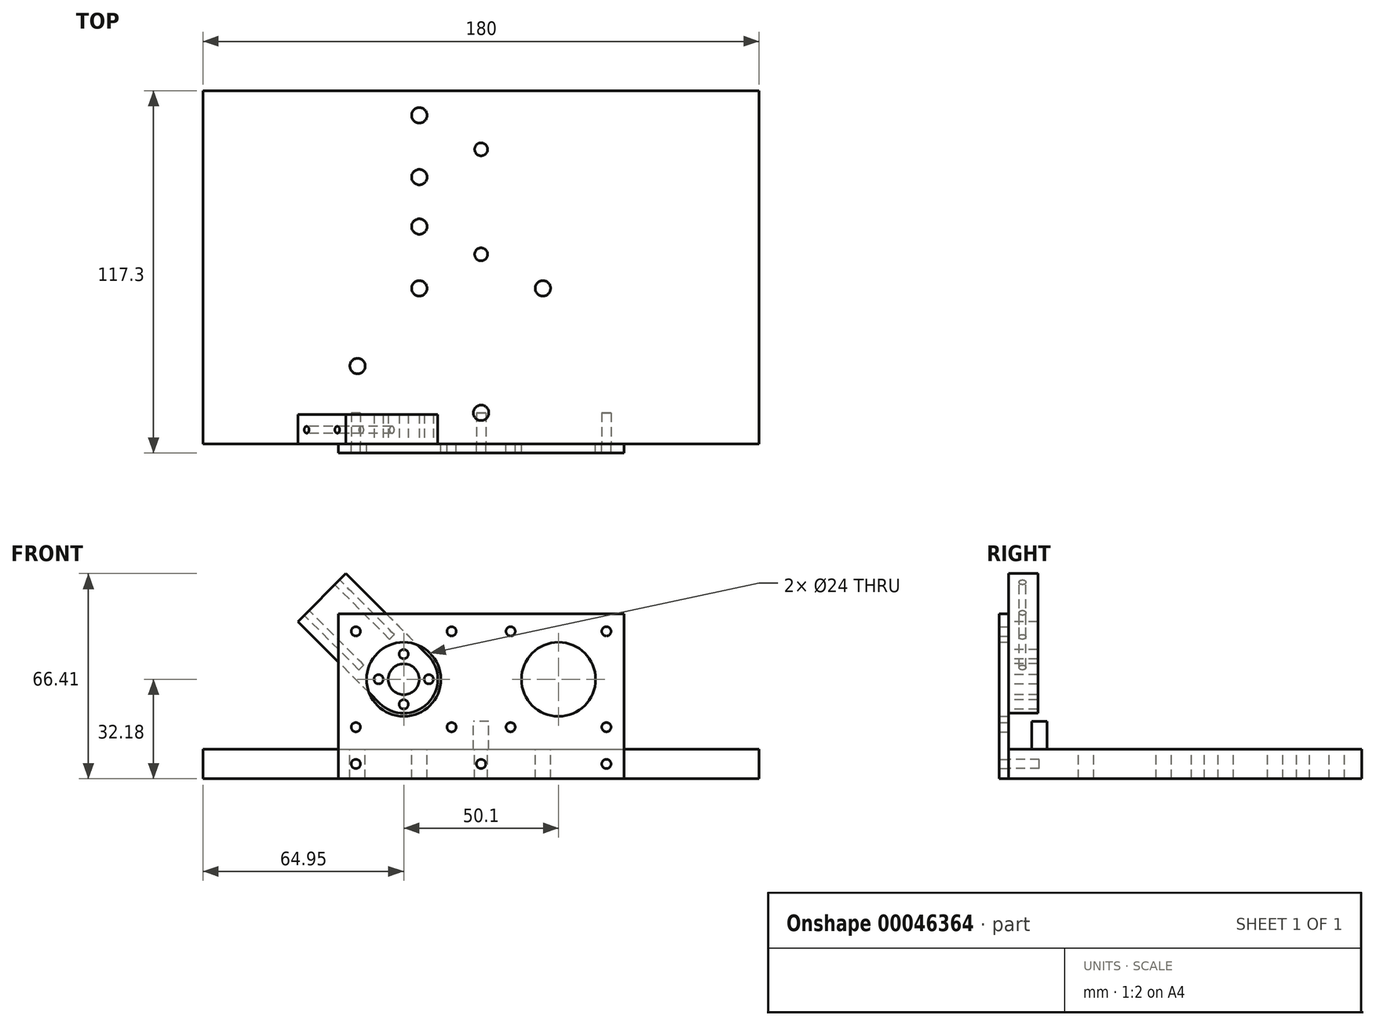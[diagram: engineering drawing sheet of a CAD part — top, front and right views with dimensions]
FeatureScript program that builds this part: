
annotation { "Feature Type Name" : "Feature", "Feature Type Description" : "" }
export const myFeature = defineFeature(function(context is Context, id is Id, definition is map)
    precondition{}
    {
        {
            var Q0;
            Q0=qCreatedBy(makeId("Front.planeOp"),FACE);
            var sketch = newSketch(context, id + "F0", { "sketchPlane" : qUnion([Q0])});
            skLineSegment(sketch, "E0", {"start": v(-110.98, 0) * mm, "end": v(110.98, 0) * mm});
            skLineSegment(sketch, "E1", {"start": v(110.98, 0) * mm, "end": v(3.5, 107.48) * mm});
            skLineSegment(sketch, "E2", {"start": v(3.5, 107.48) * mm, "end": v(-3.5, 107.48) * mm, "construction": true});
            skLineSegment(sketch, "E3", {"start": v(-3.5, 107.48) * mm, "end": v(-110.98, 0) * mm});
            skLineSegment(sketch, "E4", {"start": v(0, 0) * mm, "end": v(0, 107.48) * mm, "construction": true});
            skLineSegment(sketch, "E5", {"start": v(3.5, 107.48) * mm, "end": v(5.62, 109.6) * mm});
            skLineSegment(sketch, "E6", {"start": v(5.62, 109.6) * mm, "end": v(113.1, 2.12) * mm});
            skLineSegment(sketch, "E7", {"start": v(113.1, 2.12) * mm, "end": v(110.98, 0) * mm});
            skLineSegment(sketch, "E8", {"start": v(5.62, 109.6) * mm, "end": v(9.86, 113.84) * mm, "construction": true});
            skLineSegment(sketch, "E9", {"start": v(9.86, 113.84) * mm, "end": v(117.34, 6.36) * mm, "construction": true});
            skLineSegment(sketch, "E10", {"start": v(117.34, 6.36) * mm, "end": v(113.1, 2.12) * mm, "construction": true});
            skLineSegment(sketch, "E11.0.MirrorCS", {"start": v(-113.1, 2.12) * mm, "end": v(-110.98, 0) * mm});
            skLineSegment(sketch, "E11.1.MirrorCS", {"start": v(-117.34, 6.36) * mm, "end": v(-113.1, 2.12) * mm, "construction": true});
            skLineSegment(sketch, "E11.2.MirrorCS", {"start": v(-5.62, 109.6) * mm, "end": v(-9.86, 113.84) * mm, "construction": true});
            skLineSegment(sketch, "E11.3.MirrorCS", {"start": v(-9.86, 113.84) * mm, "end": v(-117.34, 6.36) * mm, "construction": true});
            skLineSegment(sketch, "E11.4.MirrorCS", {"start": v(-5.62, 109.6) * mm, "end": v(-113.1, 2.12) * mm});
            skLineSegment(sketch, "E11.5.MirrorCS", {"start": v(-3.5, 107.48) * mm, "end": v(-5.62, 109.6) * mm});
            skLineSegment(sketch, "E12", {"start": v(48.75, 66.47) * mm, "end": v(53, 70.71) * mm, "construction": true});
            skLineSegment(sketch, "E13.0.MirrorCS", {"start": v(-48.75, 66.47) * mm, "end": v(-53, 70.71) * mm, "construction": true});
            skLineSegment(sketch, "E14", {"start": v(97.55, 17.68) * mm, "end": v(101.79, 21.92) * mm, "construction": true});
            skLineSegment(sketch, "E15.0.MirrorCS", {"start": v(-97.55, 17.68) * mm, "end": v(-101.79, 21.92) * mm, "construction": true});
            skLineSegment(sketch, "E16", {"start": v(5.62, 109.6) * mm, "end": v(-9.86, 125.09) * mm, "construction": true});
            skLineSegment(sketch, "E17", {"start": v(-5.62, 109.6) * mm, "end": v(9.86, 125.09) * mm, "construction": true});
            skLineSegment(sketch, "E18", {"start": v(-3.5, 107.48) * mm, "end": v(-3.5, 118.8) * mm, "construction": true});
            skLineSegment(sketch, "E19", {"start": v(-9.86, 113.84) * mm, "end": v(-4.2, 119.5) * mm, "construction": true});
            skLineSegment(sketch, "E20", {"start": v(-4.2, 119.5) * mm, "end": v(-3.5, 118.8) * mm, "construction": true});
            skLineSegment(sketch, "E21.0.MirrorCS", {"start": v(3.5, 107.48) * mm, "end": v(3.5, 118.8) * mm, "construction": true});
            skLineSegment(sketch, "E21.1.MirrorCS", {"start": v(4.2, 119.5) * mm, "end": v(3.5, 118.8) * mm, "construction": true});
            skLineSegment(sketch, "E21.2.MirrorCS", {"start": v(9.86, 113.84) * mm, "end": v(4.2, 119.5) * mm, "construction": true});
            skLineSegment(sketch, "E22", {"start": v(-84.7, 9.31) * mm, "end": v(-28.13, 65.88) * mm, "construction": true});
            skPoint(sketch, "E23", {"position": v(-56.41, 37.6) * mm});
            skPoint(sketch, "E24", {"position": v(-57.24, 53.74) * mm});
            skLineSegment(sketch, "E25", {"start": v(-33.43, 60.58) * mm, "end": v(-90, 4) * mm, "construction": true});
            skLineSegment(sketch, "E26", {"start": v(-90, 4) * mm, "end": v(-10, 4) * mm, "construction": true});
            skLineSegment(sketch, "E27", {"start": v(-10, 4) * mm, "end": v(-10, 13) * mm});
            skLineSegment(sketch, "E28", {"start": v(-10, 13) * mm, "end": v(-68.27, 13) * mm, "construction": true});
            skLineSegment(sketch, "E29", {"start": v(-68.27, 13) * mm, "end": v(-27.07, 54.21) * mm, "construction": true});
            skLineSegment(sketch, "E30", {"start": v(-27.07, 54.21) * mm, "end": v(-33.43, 60.58) * mm, "construction": true});
            skLineSegment(sketch, "E31", {"start": v(-28.13, 65.88) * mm, "end": v(-36.61, 74.37) * mm, "construction": true});
            skLineSegment(sketch, "E32", {"start": v(-84.7, 9.31) * mm, "end": v(-93.18, 17.8) * mm, "construction": true});
            skLineSegment(sketch, "E33", {"start": v(-93.18, 17.8) * mm, "end": v(-36.61, 74.37) * mm, "construction": true});
            skLineSegment(sketch, "E34.0.MirrorCS", {"start": v(10, 4) * mm, "end": v(10, 13) * mm});
            skLineSegment(sketch, "E35", {"start": v(-10, 13) * mm, "end": v(10, 13) * mm});
            skLineSegment(sketch, "E36", {"start": v(-10, 4) * mm, "end": v(10, 4) * mm});
            skLineSegment(sketch, "E37.0.MirrorCS", {"start": v(68.27, 13) * mm, "end": v(27.07, 54.21) * mm, "construction": true});
            skLineSegment(sketch, "E37.1.MirrorCS", {"start": v(27.07, 54.21) * mm, "end": v(33.43, 60.58) * mm, "construction": true});
            skLineSegment(sketch, "E37.2.MirrorCS", {"start": v(33.43, 60.58) * mm, "end": v(90, 4) * mm, "construction": true});
            skLineSegment(sketch, "E37.3.MirrorCS", {"start": v(90, 4) * mm, "end": v(10, 4) * mm, "construction": true});
            skLineSegment(sketch, "E37.4.MirrorCS", {"start": v(10, 13) * mm, "end": v(68.27, 13) * mm, "construction": true});
            skPoint(sketch, "E38", {"position": v(-20, 13) * mm});
            skPoint(sketch, "E39.0.MirrorP", {"position": v(20, 13) * mm});
            skLineSegment(sketch, "E40.bottom", {"start": v(-90, 4) * mm, "end": v(90, 4) * mm});
            skLineSegment(sketch, "E40.top", {"start": v(-90, -5.52) * mm, "end": v(90, -5.52) * mm});
            skLineSegment(sketch, "E40.left", {"start": v(-90, 4) * mm, "end": v(-90, -5.52) * mm});
            skLineSegment(sketch, "E40.right", {"start": v(90, 4) * mm, "end": v(90, -5.52) * mm});
            skLineSegment(sketch, "E41", {"start": v(-50.76, 60.22) * mm, "end": v(-42.27, 51.74) * mm, "construction": true});
            skSolve(sketch);
        }
        {
            var Q0;
            {var subQ2=sQuery(id+"F0.wireOp",EDGE,"E27");Q0=makeQuery(id+"F0.imprint","IMPRINT",FACE,{"disambiguationData":[TD([[makeQuery(id+"F0.imprint","IMPRINT",EDGE,{"derivedFrom":subQ2}),-1.0]])]});}
            var Q1;
            {var subQ8=sQuery(id+"F0.wireOp",EDGE,"E34.0.MirrorCS");Q1=makeQuery(id+"F0.imprint","IMPRINT",FACE,{"disambiguationData":[TD([[makeQuery(id+"F0.imprint","IMPRINT",EDGE,{"derivedFrom":subQ8}),1.0]])]});}
            extrude(context, id + "F1", {"entities" : qUnion([Q0, Q1]), "oppositeDirection" : true, "depth" : 54 * mm});
        }
        {
            var Q0;
            {var subQ3=sQuery(id+"F0.wireOp",EDGE,"E40.top");Q0=makeQuery(id+"F0.imprint","IMPRINT",FACE,{"disambiguationData":[TD([[makeQuery(id+"F0.imprint","IMPRINT",EDGE,{"derivedFrom":subQ3}),1.0]])]});}
            var Q1;
            {var subQ1=sQuery(id+"F0.wireOp",EDGE,"E0");var subQ5=sQuery(id+"F0.wireOp",EDGE,"E40.left");var subQ6=makeQuery(id+"F0.imprint","INTERSECT",VERTEX,{"derivedFrom":[subQ1,subQ5]});Q1=makeQuery(id+"F0.imprint","IMPRINT",FACE,{"disambiguationData":[TD([[makeQuery(id+"F0.imprint","IMPRINT",EDGE,{"disambiguationData":[TD([[subQ6,-1.0]])],"derivedFrom":subQ1}),1.0]])]});}
            extrude(context, id + "F2", {"entities" : qUnion([Q0, Q1]), "oppositeDirection" : true, "depth" : 114.3 * mm});
        }
        {
            var Q0;
            Q0=makeQuery(id+"F1.opExtrude","SWEPT_FACE",FACE,{"disambiguationData":[OSD([sQuery(id+"F0.wireOp",EDGE,"E35")])]});
            var sketch = newSketch(context, id + "F3", { "sketchPlane" : qUnion([Q0])});
            skCircle(sketch, "E42", {"center": v(20, 50.3) * mm, "radius": 2.5 * mm});
            skCircle(sketch, "E43", {"center": v(-20, 50.3) * mm, "radius": 2.5 * mm});
            skLineSegment(sketch, "E44", {"start": v(0, 0) * mm, "end": v(0, 54) * mm, "construction": true});
            skLineSegment(sketch, "E45", {"start": v(-10, 27) * mm, "end": v(10, 27) * mm, "construction": true});
            skCircle(sketch, "E46", {"center": v(-20, 70.3) * mm, "radius": 2.5 * mm});
            skCircle(sketch, "E47", {"center": v(-20, 86.3) * mm, "radius": 2.5 * mm});
            skCircle(sketch, "E48", {"center": v(-20, 106.3) * mm, "radius": 2.5 * mm});
            skCircle(sketch, "E49.0.MirrorC", {"center": v(20, 70.3) * mm, "radius": 2.5 * mm});
            skCircle(sketch, "E49.1.MirrorC", {"center": v(20, 86.3) * mm, "radius": 2.5 * mm});
            skCircle(sketch, "E49.2.MirrorC", {"center": v(20, 106.3) * mm, "radius": 2.5 * mm});
            skCircle(sketch, "E50", {"center": v(-40, 25.15) * mm, "radius": 2.5 * mm});
            skLineSegment(sketch, "E51", {"start": v(-20, 50.3) * mm, "end": v(-20, 0) * mm, "construction": true});
            skPoint(sketch, "E52", {"position": v(-20, 25.15) * mm});
            skLineSegment(sketch, "E53", {"start": v(20, 86.3) * mm, "end": v(20, 70.3) * mm, "construction": true});
            skLineSegment(sketch, "E54", {"start": v(-20, 86.3) * mm, "end": v(-20, 70.3) * mm, "construction": true});
            skLineSegment(sketch, "E55", {"start": v(-20, 78.3) * mm, "end": v(20, 78.3) * mm, "construction": true});
            skCircle(sketch, "E56", {"center": v(0, 95.3) * mm, "radius": 2.1 * mm});
            skCircle(sketch, "E57", {"center": v(0, 61.3) * mm, "radius": 2.1 * mm});
            skSolve(sketch);
        }
        {
            var Q0;
            Q0=makeQuery(id+"F3.imprint","IMPRINT",FACE,{"disambiguationData":[TD([[makeQuery(id+"F3.imprint","IMPRINT",EDGE,{"derivedFrom":sQuery(id+"F3.wireOp",EDGE,"E43")}),1.0]])]});
            var Q1;
            Q1=makeQuery(id+"F3.imprint","IMPRINT",FACE,{"disambiguationData":[TD([[makeQuery(id+"F3.imprint","IMPRINT",EDGE,{"derivedFrom":sQuery(id+"F3.wireOp",EDGE,"c1587aed-859c-4511-8a7d-6d54e1cc8fba")}),1.0]])]});
            var Q2;
            Q2=makeQuery(id+"F3.imprint","IMPRINT",FACE,{"disambiguationData":[TD([[makeQuery(id+"F3.imprint","IMPRINT",EDGE,{"derivedFrom":sQuery(id+"F3.wireOp",EDGE,"E42")}),1.0]])]});
            var Q3;
            Q3=makeQuery(id+"F3.imprint","IMPRINT",FACE,{"disambiguationData":[TD([[makeQuery(id+"F3.imprint","IMPRINT",EDGE,{"derivedFrom":sQuery(id+"F3.wireOp",EDGE,"E46")}),1.0]])]});
            var Q4;
            Q4=makeQuery(id+"F3.imprint","IMPRINT",FACE,{"disambiguationData":[TD([[makeQuery(id+"F3.imprint","IMPRINT",EDGE,{"derivedFrom":sQuery(id+"F3.wireOp",EDGE,"E47")}),1.0]])]});
            var Q5;
            Q5=makeQuery(id+"F3.imprint","IMPRINT",FACE,{"disambiguationData":[TD([[makeQuery(id+"F3.imprint","IMPRINT",EDGE,{"derivedFrom":sQuery(id+"F3.wireOp",EDGE,"E48")}),1.0]])]});
            var Q6;
            Q6=makeQuery(id+"F3.imprint","IMPRINT",FACE,{"disambiguationData":[TD([[makeQuery(id+"F3.imprint","IMPRINT",EDGE,{"derivedFrom":sQuery(id+"F3.wireOp",EDGE,"E49.2.MirrorC")}),-1.0]])]});
            var Q7;
            Q7=makeQuery(id+"F3.imprint","IMPRINT",FACE,{"disambiguationData":[TD([[makeQuery(id+"F3.imprint","IMPRINT",EDGE,{"derivedFrom":sQuery(id+"F3.wireOp",EDGE,"E49.1.MirrorC")}),-1.0]])]});
            var Q8;
            Q8=makeQuery(id+"F3.imprint","IMPRINT",FACE,{"disambiguationData":[TD([[makeQuery(id+"F3.imprint","IMPRINT",EDGE,{"derivedFrom":sQuery(id+"F3.wireOp",EDGE,"E49.0.MirrorC")}),-1.0]])]});
            var Q9;
            Q9=makeQuery(id+"F3.imprint","IMPRINT",FACE,{"disambiguationData":[TD([[makeQuery(id+"F3.imprint","IMPRINT",EDGE,{"derivedFrom":sQuery(id+"F3.wireOp",EDGE,"E50")}),1.0]])]});
            var Q10;
            Q10=makeQuery(id+"F3.imprint","IMPRINT",FACE,{"disambiguationData":[TD([[makeQuery(id+"F3.imprint","IMPRINT",EDGE,{"derivedFrom":sQuery(id+"F3.wireOp",EDGE,"4af6d40a-a213-410c-9ecb-ddd685a41705.0.MirrorC")}),-1.0]])]});
            var Q11;
            Q11=makeQuery(id+"F3.imprint","IMPRINT",FACE,{"disambiguationData":[TD([[makeQuery(id+"F3.imprint","IMPRINT",EDGE,{"derivedFrom":sQuery(id+"F3.wireOp",EDGE,"E56")}),1.0]])]});
            var Q12;
            Q12=makeQuery(id+"F3.imprint","IMPRINT",FACE,{"disambiguationData":[TD([[makeQuery(id+"F3.imprint","IMPRINT",EDGE,{"derivedFrom":sQuery(id+"F3.wireOp",EDGE,"E57")}),1.0]])]});
            extrude(context, id + "F4", {"entities" : qUnion([Q0, Q1, Q2, Q3, Q4, Q5, Q6, Q7, Q8, Q9, Q10, Q11, Q12]), "operationType" : NewBodyOperationType.REMOVE, "oppositeDirection" : true, "depth" : 25 * mm});
        }
        {
            var Q0;
            Q0=qCreatedBy(makeId("Front.planeOp"),FACE);
            var sketch = newSketch(context, id + "F5", { "sketchPlane" : qUnion([Q0])});
            skLineSegment(sketch, "E58.bottom", {"start": v(-3.9, 47.8) * mm, "end": v(-46.2, 47.8) * mm});
            skLineSegment(sketch, "E58.top", {"start": v(-3.9, 5.5) * mm, "end": v(-46.2, 5.5) * mm});
            skLineSegment(sketch, "E58.left", {"start": v(-3.9, 47.8) * mm, "end": v(-3.9, 5.5) * mm});
            skLineSegment(sketch, "E58.right", {"start": v(-46.2, 47.8) * mm, "end": v(-46.2, 5.5) * mm});
            skLineSegment(sketch, "E59", {"start": v(-46.2, 26.66) * mm, "end": v(-3.9, 26.66) * mm, "construction": true});
            skLineSegment(sketch, "E60", {"start": v(-25.05, 47.8) * mm, "end": v(-25.05, 5.5) * mm, "construction": true});
            skCircle(sketch, "E61", {"center": v(-40.55, 42.16) * mm, "radius": 1.5 * mm});
            skCircle(sketch, "E62.0.MirrorC", {"center": v(-9.55, 42.16) * mm, "radius": 1.5 * mm});
            skCircle(sketch, "E63.0.MirrorC", {"center": v(-40.55, 11.16) * mm, "radius": 1.5 * mm});
            skCircle(sketch, "E64.0.MirrorC", {"center": v(-9.55, 11.16) * mm, "radius": 1.5 * mm});
            skLineSegment(sketch, "E65.0", {"start": v(0, 0) * mm, "end": v(0, 107.48) * mm, "construction": true});
            skLineSegment(sketch, "E66.0.MirrorCS", {"start": v(3.9, 47.8) * mm, "end": v(46.2, 47.8) * mm});
            skLineSegment(sketch, "E67.0.MirrorCS", {"start": v(3.9, 47.8) * mm, "end": v(3.9, 5.5) * mm});
            skLineSegment(sketch, "E68.0.MirrorCS", {"start": v(3.9, 5.5) * mm, "end": v(46.2, 5.5) * mm});
            skLineSegment(sketch, "E69.0.MirrorCS", {"start": v(46.2, 47.8) * mm, "end": v(46.2, 5.5) * mm});
            skCircle(sketch, "E70.0.MirrorC", {"center": v(40.55, 42.16) * mm, "radius": 1.5 * mm});
            skCircle(sketch, "E71.0.MirrorC", {"center": v(9.55, 42.16) * mm, "radius": 1.5 * mm});
            skCircle(sketch, "E72.0.MirrorC", {"center": v(9.55, 11.16) * mm, "radius": 1.5 * mm});
            skCircle(sketch, "E73.0.MirrorC", {"center": v(40.55, 11.16) * mm, "radius": 1.5 * mm});
            skLineSegment(sketch, "E74", {"start": v(-3.9, 47.8) * mm, "end": v(3.9, 47.8) * mm});
            skLineSegment(sketch, "E75", {"start": v(3.9, 5.5) * mm, "end": v(-3.9, 5.5) * mm});
            skLineSegment(sketch, "E76.0", {"start": v(-90, -5.52) * mm, "end": v(90, -5.52) * mm, "construction": true});
            skLineSegment(sketch, "E77.bottom", {"start": v(-46.2, 5.5) * mm, "end": v(46.2, 5.5) * mm});
            skLineSegment(sketch, "E77.top", {"start": v(-46.2, -5.52) * mm, "end": v(46.2, -5.52) * mm});
            skLineSegment(sketch, "E77.left", {"start": v(-46.2, 5.5) * mm, "end": v(-46.2, -5.52) * mm});
            skLineSegment(sketch, "E77.right", {"start": v(46.2, 5.5) * mm, "end": v(46.2, -5.52) * mm});
            skLineSegment(sketch, "E78.0", {"start": v(10, 4) * mm, "end": v(10, 13) * mm});
            skPoint(sketch, "E79", {"position": v(10, 8.5) * mm});
            skLineSegment(sketch, "E80.0", {"start": v(-90, 4) * mm, "end": v(-90, -5.52) * mm});
            skPoint(sketch, "E81", {"position": v(-90, -0.75) * mm});
            skCircle(sketch, "E82", {"center": v(0, -0.75) * mm, "radius": 1.5 * mm});
            skCircle(sketch, "E83", {"center": v(40.55, -0.75) * mm, "radius": 1.5 * mm});
            skCircle(sketch, "E84", {"center": v(-40.55, -0.75) * mm, "radius": 1.5 * mm});
            skCircle(sketch, "E85", {"center": v(-25.05, 26.66) * mm, "radius": 12 * mm});
            skCircle(sketch, "E86.0.MirrorC", {"center": v(25.05, 26.66) * mm, "radius": 12 * mm});
            skSolve(sketch);
        }
        {
            var Q0;
            Q0=qCreatedBy(makeId("Front.planeOp"),FACE);
            var sketch = newSketch(context, id + "F6", { "sketchPlane" : qUnion([Q0])});
            skCircle(sketch, "E87.0", {"center": v(-25.05, 26.66) * mm, "radius": 12 * mm});
            skCircle(sketch, "E88", {"center": v(-25.05, 26.66) * mm, "radius": 11 * mm});
            skLineSegment(sketch, "E89.0", {"start": v(-25.05, 47.8) * mm, "end": v(-25.05, 5.5) * mm, "construction": true});
            skLineSegment(sketch, "E90.0", {"start": v(-46.2, 26.66) * mm, "end": v(-3.9, 26.66) * mm, "construction": true});
            skCircle(sketch, "E91", {"center": v(-25.05, 26.66) * mm, "radius": 5 * mm});
            skLineSegment(sketch, "E92", {"start": v(-32.83, 18.88) * mm, "end": v(-59.28, 45.33) * mm});
            skLineSegment(sketch, "E93", {"start": v(-59.28, 45.33) * mm, "end": v(-43.73, 60.9) * mm});
            skLineSegment(sketch, "E94", {"start": v(-43.73, 60.9) * mm, "end": v(-17.27, 34.44) * mm});
            skLineSegment(sketch, "E95.0", {"start": v(-3.5, 107.48) * mm, "end": v(-110.98, 0) * mm});
            skLineSegment(sketch, "E96", {"start": v(-25.05, 26.66) * mm, "end": v(-36.23, 37.84) * mm, "construction": true});
            skLineSegment(sketch, "E97", {"start": v(-25.05, 26.66) * mm, "end": v(-13.87, 37.84) * mm, "construction": true});
            skCircle(sketch, "E98", {"center": v(-25.05, 34.8) * mm, "radius": 1.5 * mm});
            skCircle(sketch, "E99.0.MirrorC", {"center": v(-16.92, 26.66) * mm, "radius": 1.5 * mm});
            skCircle(sketch, "E100.0.MirrorC", {"center": v(-33.18, 26.66) * mm, "radius": 1.5 * mm});
            skCircle(sketch, "E101.0.MirrorC", {"center": v(-25.05, 18.53) * mm, "radius": 1.5 * mm});
            skSolve(sketch);
        }
        {
            var Q0;
            Q0=makeQuery(id+"F6.imprint","IMPRINT",FACE,{"disambiguationData":[TD([[makeQuery(id+"F6.imprint","IMPRINT",EDGE,{"derivedFrom":sQuery(id+"F6.wireOp",EDGE,"5af2287f-f276-41c1-868d-646f8101a97e")}),-1.0]])]});
            var Q1;
            {var subQ3=sQuery(id+"F6.wireOp",EDGE,"E93");Q1=makeQuery(id+"F6.imprint","IMPRINT",FACE,{"disambiguationData":[TD([[makeQuery(id+"F6.imprint","IMPRINT",EDGE,{"derivedFrom":subQ3}),-1.0]])]});}
            var Q2;
            {var subQ1=sQuery(id+"F6.wireOp",EDGE,"E87.0");var subQ5=sQuery(id+"F6.wireOp",EDGE,"E92");var subQ6=makeQuery(id+"F6.imprint","INTERSECT",VERTEX,{"derivedFrom":[subQ1,subQ5]});Q2=makeQuery(id+"F6.imprint","IMPRINT",FACE,{"disambiguationData":[TD([[makeQuery(id+"F6.imprint","IMPRINT",EDGE,{"disambiguationData":[TD([[subQ6,1.0]])],"derivedFrom":subQ1}),1.0]])]});}
            var Q3;
            Q3=makeQuery(id+"F6.imprint","IMPRINT",FACE,{"disambiguationData":[TD([[makeQuery(id+"F6.imprint","IMPRINT",EDGE,{"derivedFrom":sQuery(id+"F6.wireOp",EDGE,"E91")}),-1.0]])]});
            extrude(context, id + "F7", {"entities" : qUnion([Q0, Q1, Q2, Q3]), "oppositeDirection" : true, "depth" : 9.53 * mm});
        }
        {
            var Q0;
            Q0=makeQuery(id+"F5.imprint","IMPRINT",FACE,{"disambiguationData":[TD([[makeQuery(id+"F5.imprint","IMPRINT",EDGE,{"derivedFrom":sQuery(id+"F5.wireOp",EDGE,"E58.bottom")}),1.0]])]});
            var Q1;
            Q1=makeQuery(id+"F5.imprint","IMPRINT",FACE,{"disambiguationData":[TD([[makeQuery(id+"F5.imprint","IMPRINT",EDGE,{"derivedFrom":sQuery(id+"F5.wireOp",EDGE,"E66.0.MirrorCS")}),-1.0]])]});
            var Q2;
            Q2=makeQuery(id+"F5.imprint","IMPRINT",FACE,{"disambiguationData":[TD([[makeQuery(id+"F5.imprint","IMPRINT",EDGE,{"derivedFrom":sQuery(id+"F5.wireOp",EDGE,"E58.left")}),1.0]])]});
            var Q3;
            Q3=makeQuery(id+"F5.imprint","IMPRINT",FACE,{"disambiguationData":[TD([[makeQuery(id+"F5.imprint","IMPRINT",EDGE,{"derivedFrom":sQuery(id+"F5.wireOp",EDGE,"E77.top")}),1.0]])]});
            extrude(context, id + "F8", {"entities" : qUnion([Q0, Q1, Q2, Q3]), "depth" : 3 * mm});
        }
        {
            var Q0;
            Q0=makeQuery(id+"F5.imprint","IMPRINT",FACE,{"disambiguationData":[TD([[makeQuery(id+"F5.imprint","IMPRINT",EDGE,{"derivedFrom":sQuery(id+"F5.wireOp",EDGE,"E84")}),1.0]])]});
            var Q1;
            Q1=makeQuery(id+"F5.imprint","IMPRINT",FACE,{"disambiguationData":[TD([[makeQuery(id+"F5.imprint","IMPRINT",EDGE,{"derivedFrom":sQuery(id+"F5.wireOp",EDGE,"E82")}),1.0]])]});
            var Q2;
            Q2=makeQuery(id+"F5.imprint","IMPRINT",FACE,{"disambiguationData":[TD([[makeQuery(id+"F5.imprint","IMPRINT",EDGE,{"derivedFrom":sQuery(id+"F5.wireOp",EDGE,"E83")}),1.0]])]});
            var Q3;
            Q3=makeQuery(id+"F5.imprint","IMPRINT",FACE,{"disambiguationData":[TD([[makeQuery(id+"F5.imprint","IMPRINT",EDGE,{"derivedFrom":sQuery(id+"F5.wireOp",EDGE,"2a58b282-65e7-4c93-9a53-bb5f714e803d")}),1.0]])]});
            extrude(context, id + "F9", {"entities" : qUnion([Q0, Q1, Q2, Q3]), "operationType" : NewBodyOperationType.REMOVE, "oppositeDirection" : true, "depth" : 10 * mm});
        }
        {
            var Q0;
            Q0=makeQuery(id+"F1.opExtrude","SWEPT_FACE",FACE,{"disambiguationData":[OSD([sQuery(id+"F0.wireOp",EDGE,"E35")])]});
            var sketch = newSketch(context, id + "F10", { "sketchPlane" : qUnion([Q0])});
            skLineSegment(sketch, "E102", {"start": v(0, 54) * mm, "end": v(0, 44) * mm, "construction": true});
            skLineSegment(sketch, "E103", {"start": v(-10, 44) * mm, "end": v(0, 44) * mm, "construction": true});
            skLineSegment(sketch, "E104", {"start": v(0, 44) * mm, "end": v(0, 0) * mm, "construction": true});
            skLineSegment(sketch, "E105", {"start": v(0, 44) * mm, "end": v(10, 44) * mm, "construction": true});
            skCircle(sketch, "E106", {"center": v(0, 44) * mm, "radius": 2.5 * mm});
            skLineSegment(sketch, "E107", {"start": v(-10, 27) * mm, "end": v(10, 27) * mm, "construction": true});
            skCircle(sketch, "E108.0.MirrorC", {"center": v(0, 10) * mm, "radius": 2.5 * mm});
            skSolve(sketch);
        }
        {
            var Q0;
            Q0=makeQuery(id+"F10.imprint","IMPRINT",FACE,{"disambiguationData":[TD([[makeQuery(id+"F10.imprint","IMPRINT",EDGE,{"derivedFrom":sQuery(id+"F10.wireOp",EDGE,"E106")}),1.0]])]});
            var Q1;
            Q1=makeQuery(id+"F10.imprint","IMPRINT",FACE,{"disambiguationData":[TD([[makeQuery(id+"F10.imprint","IMPRINT",EDGE,{"derivedFrom":sQuery(id+"F10.wireOp",EDGE,"E108.0.MirrorC")}),-1.0]])]});
            extrude(context, id + "F11", {"entities" : qUnion([Q0, Q1]), "operationType" : NewBodyOperationType.REMOVE, "endBound" : BoundingType.UP_TO_NEXT, "oppositeDirection" : true, "depth" : 25 * mm});
        }
        {
            var Q0;
            Q0=makeQuery(id+"F7.opExtrude","SWEPT_FACE",FACE,{"disambiguationData":[OSD([sQuery(id+"F6.wireOp",EDGE,"E93")])]});
            var sketch = newSketch(context, id + "F12", { "sketchPlane" : qUnion([Q0])});
            skSolve(sketch);
        }
        {
            var Q0;
            {var subQ0=sQuery(id+"F6.wireOp",EDGE,"E93");Q0=makeQuery(id+"F12.imprint","IMPRINT",FACE,{"disambiguationData":[TD([[makeQuery(id+"F12.imprint","IMPRINT",EDGE,{"derivedFrom":makeQuery(id+"F7.opExtrude","CAP_EDGE",EDGE,{"disambiguationData":[OSD([subQ0])],"isStart":true})}),1.0]])]});}
            var sketch = newSketch(context, id + "F13", { "sketchPlane" : qUnion([Q0])});
            skCircle(sketch, "E109", {"center": v(-4.53, -5.86) * mm, "radius": 1.1 * mm});
            skCircle(sketch, "E110", {"center": v(-4.53, 8.14) * mm, "radius": 1.1 * mm});
            skLineSegment(sketch, "E111.0", {"start": v(-9.53, -9.86) * mm, "end": v(-9.53, 12.14) * mm});
            skLineSegment(sketch, "E112.0", {"start": v(0, -9.86) * mm, "end": v(0, 12.14) * mm});
            skSolve(sketch);
        }
        {
            var Q0;
            Q0=makeQuery(id+"F13.imprint","IMPRINT",FACE,{"disambiguationData":[TD([[makeQuery(id+"F13.imprint","IMPRINT",EDGE,{"derivedFrom":sQuery(id+"F13.wireOp",EDGE,"E109")}),1.0]])]});
            var Q1;
            Q1=makeQuery(id+"F13.imprint","IMPRINT",FACE,{"disambiguationData":[TD([[makeQuery(id+"F13.imprint","IMPRINT",EDGE,{"derivedFrom":sQuery(id+"F13.wireOp",EDGE,"E110")}),1.0]])]});
            extrude(context, id + "F14", {"entities" : qUnion([Q0, Q1]), "operationType" : NewBodyOperationType.REMOVE, "oppositeDirection" : true, "depth" : 25 * mm});
        }
    });
